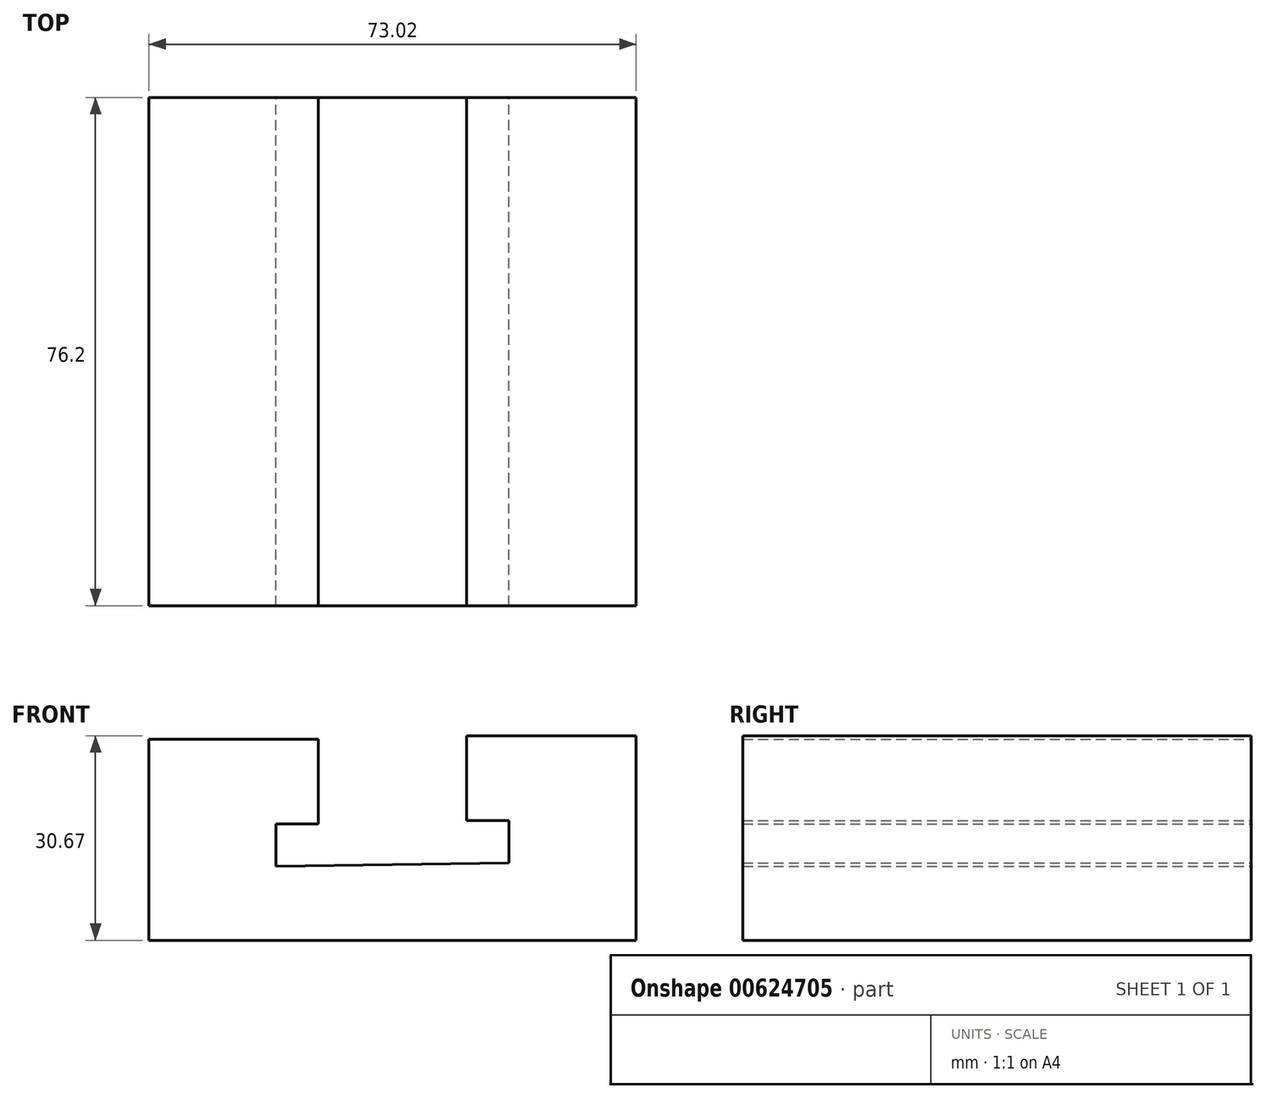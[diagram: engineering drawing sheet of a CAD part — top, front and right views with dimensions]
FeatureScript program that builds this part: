
annotation { "Feature Type Name" : "Feature", "Feature Type Description" : "" }
export const myFeature = defineFeature(function(context is Context, id is Id, definition is map)
    precondition{}
    {
        {
            var Q0;
            Q0=qCreatedBy(makeId("Front.planeOp"),FACE);
            var sketch = newSketch(context, id + "F0", { "sketchPlane" : qUnion([Q0])});
            skLineSegment(sketch, "E0", {"start": v(-26.61, 11.15) * mm, "end": v(-26.61, -19) * mm});
            skLineSegment(sketch, "E1", {"start": v(-26.61, -19) * mm, "end": v(46.41, -19) * mm});
            skLineSegment(sketch, "E2", {"start": v(46.41, -19) * mm, "end": v(46.41, 11.66) * mm});
            skLineSegment(sketch, "E3", {"start": v(-26.61, 11.15) * mm, "end": v(-1.21, 11.15) * mm});
            skLineSegment(sketch, "E4", {"start": v(-1.21, 11.15) * mm, "end": v(-1.21, -1.55) * mm});
            skLineSegment(sketch, "E5", {"start": v(-1.21, -1.55) * mm, "end": v(-7.56, -1.55) * mm});
            skLineSegment(sketch, "E6", {"start": v(46.41, 11.66) * mm, "end": v(21.01, 11.66) * mm});
            skLineSegment(sketch, "E7", {"start": v(21.01, 11.66) * mm, "end": v(21.01, -1.04) * mm});
            skLineSegment(sketch, "E8", {"start": v(21.01, -1.04) * mm, "end": v(27.36, -1.04) * mm});
            skLineSegment(sketch, "E9", {"start": v(-7.56, -1.55) * mm, "end": v(-7.56, -7.9) * mm});
            skLineSegment(sketch, "E10", {"start": v(27.36, -1.04) * mm, "end": v(27.36, -7.39) * mm});
            skLineSegment(sketch, "E11", {"start": v(-7.56, -7.9) * mm, "end": v(27.36, -7.39) * mm});
            skSolve(sketch);
        }
        {
            var Q0;
            Q0=makeQuery(id+"F0.imprint","IMPRINT",FACE,{"disambiguationData":[TD([[makeQuery(id+"F0.imprint","IMPRINT",EDGE,{"derivedFrom":sQuery(id+"F0.wireOp",EDGE,"E0")}),1.0]])]});
            extrude(context, id + "F1", {"entities" : qUnion([Q0]), "depth" : 76.2 * mm, "offsetDistance" : 25.4 * mm});
        }
    });
